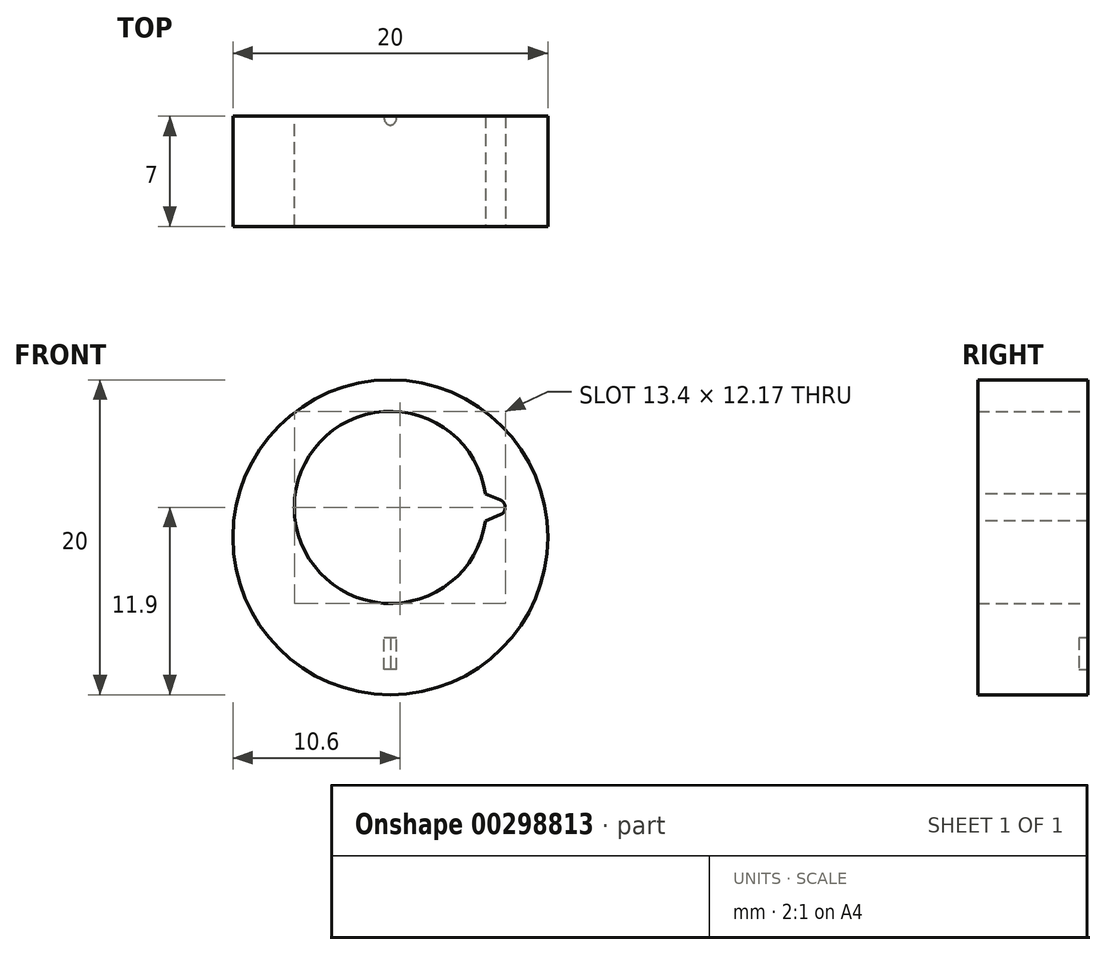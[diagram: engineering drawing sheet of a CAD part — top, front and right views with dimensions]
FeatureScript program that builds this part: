
annotation { "Feature Type Name" : "Feature", "Feature Type Description" : "" }
export const myFeature = defineFeature(function(context is Context, id is Id, definition is map)
    precondition{}
    {
        {
            var Q0;
            Q0=qCreatedBy(makeId("Front.planeOp"),FACE);
            var sketch = newSketch(context, id + "F0", { "sketchPlane" : qUnion([Q0])});
            skCircle(sketch, "E0", {"center": v(0, 0) * mm, "radius": 6.1 * mm});
            skCircle(sketch, "E1", {"center": v(0, -1.9) * mm, "radius": 10 * mm});
            skSolve(sketch);
        }
        {
            var Q0;
            Q0=makeQuery(id+"F0.imprint","IMPRINT",FACE,{"disambiguationData":[TD([[makeQuery(id+"F0.imprint","IMPRINT",EDGE,{"derivedFrom":sQuery(id+"F0.wireOp",EDGE,"E0")}),-1.0]])]});
            extrude(context, id + "F1", {"entities" : qUnion([Q0]), "depth" : 7 * mm});
        }
        {
            var Q0;
            Q0=makeQuery(id+"F1.opExtrude","CAP_FACE",FACE,{"disambiguationData":[OSD([sQuery(id+"F0.wireOp",EDGE,"E0"),sQuery(id+"F0.wireOp",EDGE,"E1")])],"isStart":false});
            var sketch = newSketch(context, id + "F2", { "sketchPlane" : qUnion([Q0])});
            skLineSegment(sketch, "E2", {"start": v(6.04, 0.86) * mm, "end": v(7, 0.46) * mm});
            skLineSegment(sketch, "E3", {"start": v(7, -0.46) * mm, "end": v(6.04, -0.86) * mm});
            skArc(sketch, "E4.filletArc", {"start": v(7, -0.46) * mm, "mid": v(7.3, 0) * mm, "end": v(7, 0.46) * mm});
            skSolve(sketch);
        }
        {
            var Q0;
            {var subQ0=sQuery(id+"F2.wireOp",EDGE,"E2");Q0=makeQuery(id+"F2.imprint","IMPRINT",FACE,{"disambiguationData":[TD([[makeQuery(id+"F2.imprint","IMPRINT",EDGE,{"derivedFrom":subQ0}),-1.0]])]});}
            extrude(context, id + "F3", {"entities" : qUnion([Q0]), "operationType" : NewBodyOperationType.REMOVE, "oppositeDirection" : true, "depth" : 7 * mm});
        }
        {
            var Q0;
            Q0=makeQuery(id+"F1.opExtrude","CAP_FACE",FACE,{"disambiguationData":[OSD([sQuery(id+"F0.wireOp",EDGE,"E0"),sQuery(id+"F0.wireOp",EDGE,"E1")])],"isStart":true});
            var sketch = newSketch(context, id + "F4", { "sketchPlane" : qUnion([Q0])});
            skLineSegment(sketch, "E5.bottom", {"start": v(-0.4, -10.3) * mm, "end": v(0.4, -10.3) * mm});
            skLineSegment(sketch, "E5.top", {"start": v(-0.4, -8.3) * mm, "end": v(0.4, -8.3) * mm});
            skLineSegment(sketch, "E5.left", {"start": v(-0.4, -10.3) * mm, "end": v(-0.4, -8.3) * mm});
            skLineSegment(sketch, "E5.right", {"start": v(0.4, -10.3) * mm, "end": v(0.4, -8.3) * mm});
            skPoint(sketch, "E5.middle", {"position": v(0, -9.3) * mm});
            skSolve(sketch);
        }
        {
            var Q0;
            Q0=makeQuery(id+"F4.imprint","IMPRINT",FACE,{"disambiguationData":[TD([[makeQuery(id+"F4.imprint","IMPRINT",EDGE,{"derivedFrom":sQuery(id+"F4.wireOp",EDGE,"E5.bottom")}),1.0]])]});
            extrude(context, id + "F5", {"entities" : qUnion([Q0]), "operationType" : NewBodyOperationType.REMOVE, "oppositeDirection" : true, "depth" : 0.6 * mm});
        }
        {
            var Q0;
            Q0=makeQuery(id+"F5.boolean.opBoolean","COPY",EDGE,{"derivedFrom":makeQuery(id+"F5.opExtrude","CAP_EDGE",EDGE,{"disambiguationData":[OSD([sQuery(id+"F4.wireOp",EDGE,"E5.left")])],"isStart":false})});
            var Q1;
            Q1=makeQuery(id+"F5.boolean.opBoolean","COPY",EDGE,{"derivedFrom":makeQuery(id+"F5.opExtrude","CAP_EDGE",EDGE,{"disambiguationData":[OSD([sQuery(id+"F4.wireOp",EDGE,"E5.right")])],"isStart":false})});
            fillet(context, id + "F6", {"entities" : qUnion([Q0, Q1]), "radius" : 0.5 * mm, "tangentPropagation" : true, "allowEdgeOverflow" : false});
        }
    });
